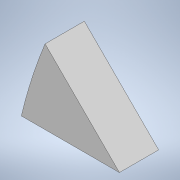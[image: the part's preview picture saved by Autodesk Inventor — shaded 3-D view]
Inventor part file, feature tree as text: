
AUTODESK INVENTOR PART (.ipt)
format: ipt  version: 2021.2 (Build 252289000, 289)  size: 94,720 bytes
history: native  units: in
note: dims shown in document units (in); Inventor stores cm internally (conversion verified against a paired STEP export)
features: extrude x1, sketch x1
ambient origin geometry x8: Origin, YZ Plane, XZ Plane, XY Plane, X Axis, Y Axis, Z Axis, Center Point
bodies: Solid1 (feature_tree)
feature tree (2):
  extrude  "Extrusion1"  Depth=13.0in
  sketch  "Sketch1"  dims[d0=12.0in d1=13.0in d2=2.5in d3=45.0deg d4=3.0in d5=1.0in d6=0.0in]
